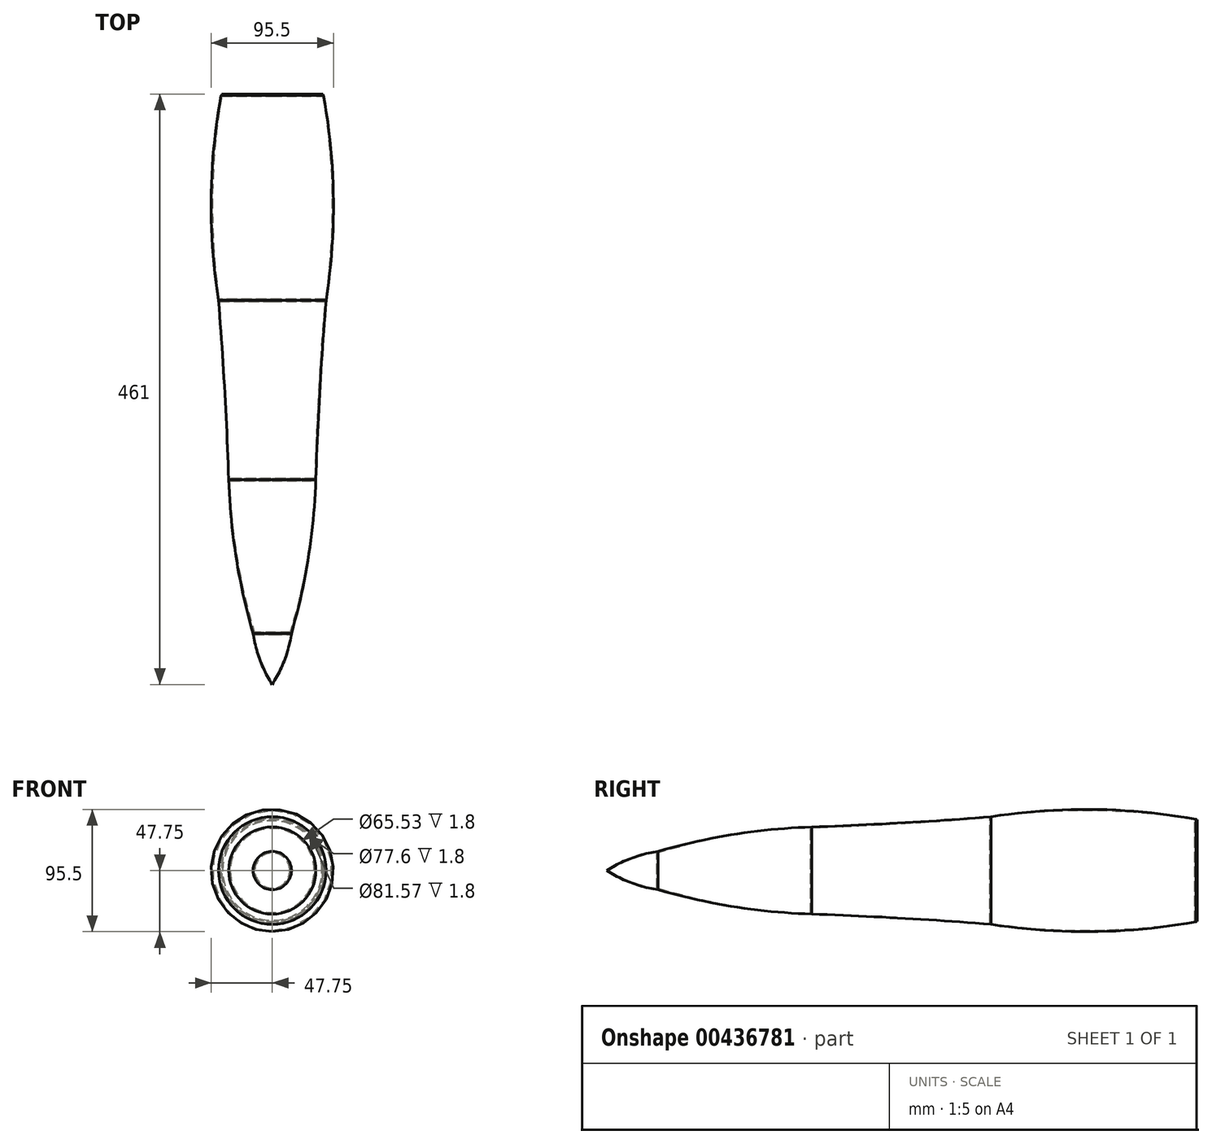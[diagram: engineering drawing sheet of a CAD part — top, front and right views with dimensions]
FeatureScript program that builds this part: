
annotation { "Feature Type Name" : "Feature", "Feature Type Description" : "" }
export const myFeature = defineFeature(function(context is Context, id is Id, definition is map)
    precondition{}
    {
        {
            var Q0;
            Q0=qCreatedBy(makeId("Right.planeOp"),FACE);
            var sketch = newSketch(context, id + "F0", { "sketchPlane" : qUnion([Q0])});
            skLineSegment(sketch, "E0", {"start": v(62.68, 0) * mm, "end": v(250.75, 0) * mm});
            skSolve(sketch);
        }
        {
            var Q0;
            Q0=qCreatedBy(makeId("Right.planeOp"),FACE);
            var sketch = newSketch(context, id + "F1", { "sketchPlane" : qUnion([Q0])});
            skArc(sketch, "E1", {"start": v(-80, -42) * mm, "mid": v(0.08, -47.71) * mm, "end": v(80, -40) * mm});
            skLineSegment(sketch, "E2", {"start": v(-80, -42) * mm, "end": v(-80, -41.6) * mm});
            skLineSegment(sketch, "E3", {"start": v(-80, -41.6) * mm, "end": v(-81, -41.49) * mm});
            skLineSegment(sketch, "E4", {"start": v(-81, -41.49) * mm, "end": v(-81, -40.79) * mm});
            skLineSegment(sketch, "E5", {"start": v(-81, -40.79) * mm, "end": v(-79.2, -40.79) * mm});
            skLineSegment(sketch, "E6", {"start": v(-79.2, -40.79) * mm, "end": v(-79.2, -41.59) * mm});
            skLineSegment(sketch, "E7", {"start": v(80, -40) * mm, "end": v(80, -39.6) * mm});
            skLineSegment(sketch, "E8", {"start": v(80, -39.6) * mm, "end": v(81, -39.6) * mm});
            skLineSegment(sketch, "E9", {"start": v(81, -39.6) * mm, "end": v(81, -38.8) * mm});
            skLineSegment(sketch, "E10", {"start": v(81, -38.8) * mm, "end": v(79.2, -38.8) * mm});
            skLineSegment(sketch, "E11", {"start": v(79.2, -38.8) * mm, "end": v(79.2, -39.6) * mm});
            skArc(sketch, "E12", {"start": v(-79.2, -41.59) * mm, "mid": v(0.08, -46.66) * mm, "end": v(79.2, -39.6) * mm});
            skSolve(sketch);
        }
        {
            var Q0;
            Q0 = qSketchRegion(id + "F1", true);
            var Q1;
            Q1=sQuery(id+"F0.wireOp",EDGE,"E0");
            revolve(context, id + "F2", {"entities" : qUnion([Q0]), "axis" : qUnion([Q1]), "revolveType" : RevolveType.FULL});
        }
        {
            var Q0;
            Q0=qCreatedBy(makeId("Right.planeOp"),FACE);
            var sketch = newSketch(context, id + "F3", { "sketchPlane" : qUnion([Q0])});
            skArc(sketch, "E13", {"start": v(-80, -42) * mm, "mid": v(-149.95, -37.18) * mm, "end": v(-220, -34) * mm});
            skLineSegment(sketch, "E14", {"start": v(-80, -42) * mm, "end": v(-80, -41.6) * mm});
            skLineSegment(sketch, "E15", {"start": v(-80, -41.6) * mm, "end": v(-81, -41.49) * mm});
            skLineSegment(sketch, "E16", {"start": v(-220, -34) * mm, "end": v(-220, -33.6) * mm});
            skLineSegment(sketch, "E17", {"start": v(-220, -33.6) * mm, "end": v(-221, -33.57) * mm});
            skLineSegment(sketch, "E18", {"start": v(-221, -33.57) * mm, "end": v(-221, -32.77) * mm});
            skLineSegment(sketch, "E19", {"start": v(-221, -32.77) * mm, "end": v(-219.2, -32.77) * mm});
            skLineSegment(sketch, "E20", {"start": v(-219.2, -32.77) * mm, "end": v(-219.2, -33.6) * mm});
            skArc(sketch, "E21", {"start": v(-81, -41.49) * mm, "mid": v(-150.04, -36.59) * mm, "end": v(-219.2, -33.6) * mm});
            skSolve(sketch);
        }
        {
            var Q0;
            Q0 = qSketchRegion(id + "F3", true);
            var Q1;
            Q1=sQuery(id+"F0.wireOp",EDGE,"E0");
            revolve(context, id + "F4", {"entities" : qUnion([Q0]), "axis" : qUnion([Q1]), "revolveType" : RevolveType.FULL});
        }
        {
            var Q0;
            Q0=qCreatedBy(makeId("Right.planeOp"),FACE);
            var sketch = newSketch(context, id + "F5", { "sketchPlane" : qUnion([Q0])});
            skArc(sketch, "E22", {"start": v(-340, -15) * mm, "mid": v(-280.6, -28.25) * mm, "end": v(-220, -34) * mm});
            skLineSegment(sketch, "E23", {"start": v(-220, -34) * mm, "end": v(-220, -33.6) * mm});
            skLineSegment(sketch, "E24", {"start": v(-220, -33.6) * mm, "end": v(-221, -33.57) * mm});
            skLineSegment(sketch, "E25", {"start": v(-340, -15) * mm, "end": v(-340, -14.6) * mm});
            skLineSegment(sketch, "E26", {"start": v(-340, -14.6) * mm, "end": v(-340.98, -14.43) * mm});
            skLineSegment(sketch, "E27", {"start": v(-340.98, -14.43) * mm, "end": v(-340.98, -13.63) * mm});
            skLineSegment(sketch, "E28", {"start": v(-340.98, -13.63) * mm, "end": v(-339.21, -13.94) * mm});
            skArc(sketch, "E29", {"start": v(-339.21, -13.94) * mm, "mid": v(-280.74, -27.59) * mm, "end": v(-221, -33.57) * mm});
            skSolve(sketch);
        }
        {
            var Q0;
            Q0 = qSketchRegion(id + "F5", true);
            var Q1;
            Q1=sQuery(id+"F0.wireOp",EDGE,"E0");
            revolve(context, id + "F6", {"entities" : qUnion([Q0]), "axis" : qUnion([Q1]), "revolveType" : RevolveType.FULL});
        }
        {
            var Q0;
            Q0=qCreatedBy(makeId("Right.planeOp"),FACE);
            var sketch = newSketch(context, id + "F7", { "sketchPlane" : qUnion([Q0])});
            skArc(sketch, "E30", {"start": v(-340, 15) * mm, "mid": v(-360.81, 9.66) * mm, "end": v(-380, 0) * mm});
            skLineSegment(sketch, "E31", {"start": v(-340, 15) * mm, "end": v(-340, 14.6) * mm});
            skLineSegment(sketch, "E32", {"start": v(-340, 14.6) * mm, "end": v(-340.98, 14.43) * mm});
            skArc(sketch, "E33", {"start": v(-340.98, 14.43) * mm, "mid": v(-360.87, 9.02) * mm, "end": v(-379.4, 0) * mm});
            skLineSegment(sketch, "E34", {"start": v(-380, 0) * mm, "end": v(-379.4, 0) * mm});
            skSolve(sketch);
        }
        {
            var Q0;
            Q0 = qSketchRegion(id + "F7", true);
            var Q1;
            Q1=sQuery(id+"F0.wireOp",EDGE,"E0");
            revolve(context, id + "F8", {"entities" : qUnion([Q0]), "axis" : qUnion([Q1]), "revolveType" : RevolveType.FULL});
        }
    });
